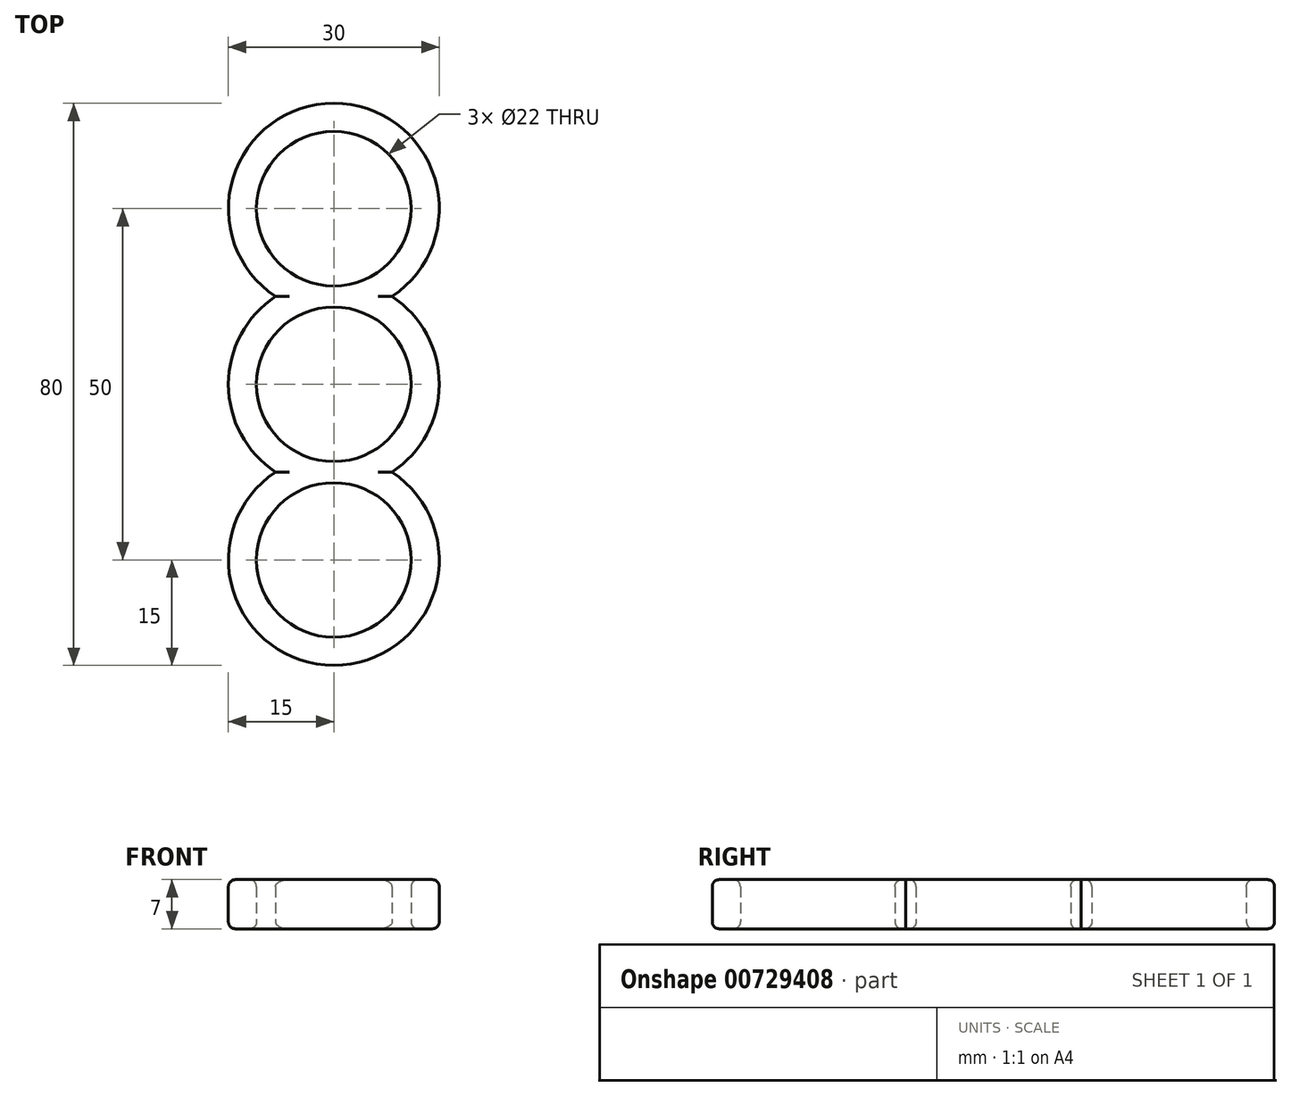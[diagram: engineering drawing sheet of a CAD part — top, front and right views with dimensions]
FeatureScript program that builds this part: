
annotation { "Feature Type Name" : "Feature", "Feature Type Description" : "" }
export const myFeature = defineFeature(function(context is Context, id is Id, definition is map)
    precondition{}
    {
        {
            var Q0;
            Q0=qCreatedBy(makeId("Top.planeOp"),FACE);
            var sketch = newSketch(context, id + "F0", { "sketchPlane" : qUnion([Q0])});
            skArc(sketch, "E0", {"start": v(-8.3, 12.5) * mm, "mid": v(-15, 0) * mm, "end": v(-8.3, -12.5) * mm});
            skCircle(sketch, "E1", {"center": v(0, 0) * mm, "radius": 11 * mm});
            skLineSegment(sketch, "E2", {"start": v(0, 10) * mm, "end": v(0, 11) * mm});
            skLineSegment(sketch, "E3", {"start": v(0, -10) * mm, "end": v(0, -11) * mm});
            skCircle(sketch, "E4", {"center": v(0, 25) * mm, "radius": 11 * mm});
            skArc(sketch, "E5", {"start": v(8.3, 12.5) * mm, "mid": v(0, 40) * mm, "end": v(-8.3, 12.5) * mm});
            skArc(sketch, "E6", {"start": v(-8.3, -12.5) * mm, "mid": v(0, -40) * mm, "end": v(8.3, -12.5) * mm});
            skCircle(sketch, "E7", {"center": v(0, -25) * mm, "radius": 11 * mm});
            skLineSegment(sketch, "E8.trimOffspring", {"start": v(0, -14) * mm, "end": v(0, -15) * mm});
            skArc(sketch, "E9.trimOffspring", {"start": v(8.3, -12.5) * mm, "mid": v(15, 0) * mm, "end": v(8.3, 12.5) * mm});
            skSolve(sketch);
        }
        {
            var Q0;
            Q0 = qSketchRegion(id + "F0", true);
            extrude(context, id + "F1", {"entities" : qUnion([Q0]), "depth" : 7 * mm, "offsetDistance" : 25 * mm});
        }
        {
            var Q0;
            Q0=makeQuery(id+"F1.opExtrude","CAP_EDGE",EDGE,{"disambiguationData":[OSD([sQuery(id+"F0.wireOp",EDGE,"E6")])],"isStart":true});
            var Q1;
            Q1=makeQuery(id+"F1.opExtrude","CAP_EDGE",EDGE,{"disambiguationData":[OSD([sQuery(id+"F0.wireOp",EDGE,"E7")])],"isStart":true});
            var Q2;
            Q2=makeQuery(id+"F1.opExtrude","CAP_EDGE",EDGE,{"disambiguationData":[OSD([sQuery(id+"F0.wireOp",EDGE,"E0")])],"isStart":true});
            var Q3;
            Q3=makeQuery(id+"F1.opExtrude","CAP_EDGE",EDGE,{"disambiguationData":[OSD([sQuery(id+"F0.wireOp",EDGE,"E1")])],"isStart":true});
            var Q4;
            Q4=makeQuery(id+"F1.opExtrude","CAP_EDGE",EDGE,{"disambiguationData":[OSD([sQuery(id+"F0.wireOp",EDGE,"E9.trimOffspring")])],"isStart":true});
            var Q5;
            Q5=makeQuery(id+"F1.opExtrude","CAP_EDGE",EDGE,{"disambiguationData":[OSD([sQuery(id+"F0.wireOp",EDGE,"E5")])],"isStart":true});
            var Q6;
            Q6=makeQuery(id+"F1.opExtrude","CAP_EDGE",EDGE,{"disambiguationData":[OSD([sQuery(id+"F0.wireOp",EDGE,"E4")])],"isStart":true});
            fillet(context, id + "F2", {"entities" : qUnion([Q0, Q1, Q2, Q3, Q4, Q5, Q6]), "radius" : 1 * mm, "tangentPropagation" : true, "allowEdgeOverflow" : false});
        }
        {
            var Q0;
            Q0=makeQuery(id+"F1.opExtrude","CAP_EDGE",EDGE,{"disambiguationData":[OSD([sQuery(id+"F0.wireOp",EDGE,"E6")])],"isStart":false});
            var Q1;
            Q1=makeQuery(id+"F1.opExtrude","CAP_EDGE",EDGE,{"disambiguationData":[OSD([sQuery(id+"F0.wireOp",EDGE,"E7")])],"isStart":false});
            var Q2;
            Q2=makeQuery(id+"F1.opExtrude","CAP_FACE",FACE,{"disambiguationData":[OSD([sQuery(id+"F0.wireOp",EDGE,"E0"),sQuery(id+"F0.wireOp",EDGE,"E1"),sQuery(id+"F0.wireOp",EDGE,"E4"),sQuery(id+"F0.wireOp",EDGE,"E5"),sQuery(id+"F0.wireOp",EDGE,"E6"),sQuery(id+"F0.wireOp",EDGE,"E7"),sQuery(id+"F0.wireOp",EDGE,"E9.trimOffspring")])],"isStart":false});
            var Q3;
            Q3=makeQuery(id+"F1.opExtrude","CAP_EDGE",EDGE,{"disambiguationData":[OSD([sQuery(id+"F0.wireOp",EDGE,"E9.trimOffspring")])],"isStart":false});
            var Q4;
            Q4=makeQuery(id+"F1.opExtrude","CAP_EDGE",EDGE,{"disambiguationData":[OSD([sQuery(id+"F0.wireOp",EDGE,"E4")])],"isStart":false});
            var Q5;
            Q5=makeQuery(id+"F1.opExtrude","CAP_EDGE",EDGE,{"disambiguationData":[OSD([sQuery(id+"F0.wireOp",EDGE,"E1")])],"isStart":false});
            var Q6;
            Q6=makeQuery(id+"F1.opExtrude","CAP_EDGE",EDGE,{"disambiguationData":[OSD([sQuery(id+"F0.wireOp",EDGE,"E0")])],"isStart":false});
            var Q7;
            Q7=makeQuery(id+"F1.opExtrude","CAP_EDGE",EDGE,{"disambiguationData":[OSD([sQuery(id+"F0.wireOp",EDGE,"E5")])],"isStart":false});
            fillet(context, id + "F3", {"entities" : qUnion([Q0, Q1, Q2, Q3, Q4, Q5, Q6, Q7]), "radius" : 1 * mm, "tangentPropagation" : true, "allowEdgeOverflow" : false});
        }
    });
